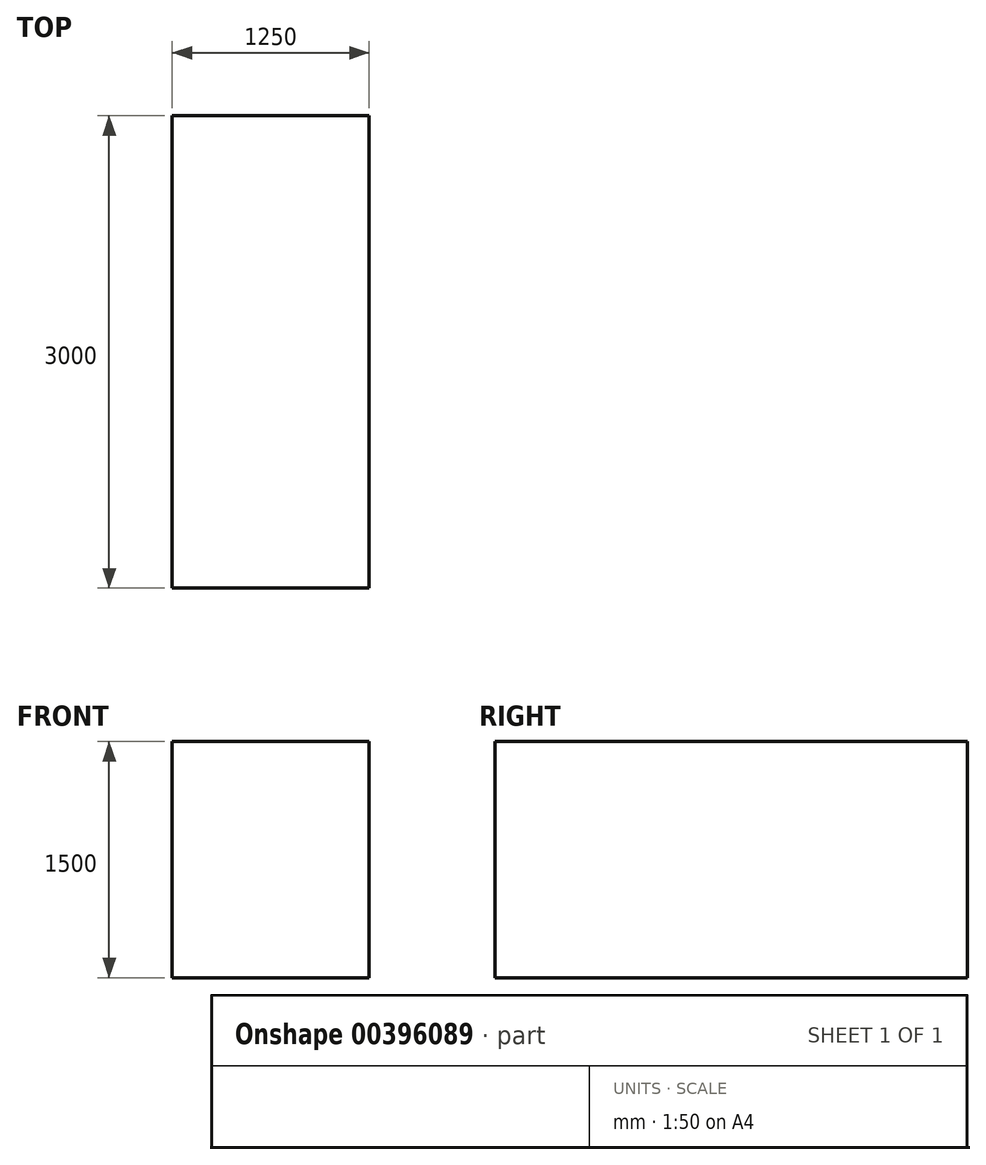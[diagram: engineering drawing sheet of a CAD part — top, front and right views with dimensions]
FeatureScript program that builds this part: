
annotation { "Feature Type Name" : "Feature", "Feature Type Description" : "" }
export const myFeature = defineFeature(function(context is Context, id is Id, definition is map)
    precondition{}
    {
        {
            var Q0;
            Q0=qCreatedBy(makeId("Top.planeOp"),FACE);
            var sketch = newSketch(context, id + "F0", { "sketchPlane" : qUnion([Q0])});
            skLineSegment(sketch, "E0.bottom", {"start": v(0, 0) * mm, "end": v(1250, 0) * mm});
            skLineSegment(sketch, "E0.top", {"start": v(0, 3000) * mm, "end": v(1250, 3000) * mm});
            skLineSegment(sketch, "E0.left", {"start": v(0, 0) * mm, "end": v(0, 3000) * mm});
            skLineSegment(sketch, "E0.right", {"start": v(1250, 0) * mm, "end": v(1250, 3000) * mm});
            skSolve(sketch);
        }
        {
            var Q0;
            Q0=makeQuery(id+"F0.imprint","IMPRINT",FACE,{"disambiguationData":[TD([[makeQuery(id+"F0.imprint","IMPRINT",EDGE,{"derivedFrom":sQuery(id+"F0.wireOp",EDGE,"E0.bottom")}),1.0]])]});
            extrude(context, id + "F1", {"entities" : qUnion([Q0]), "depth" : 1500 * mm, "offsetDistance" : 25 * mm});
        }
    });
